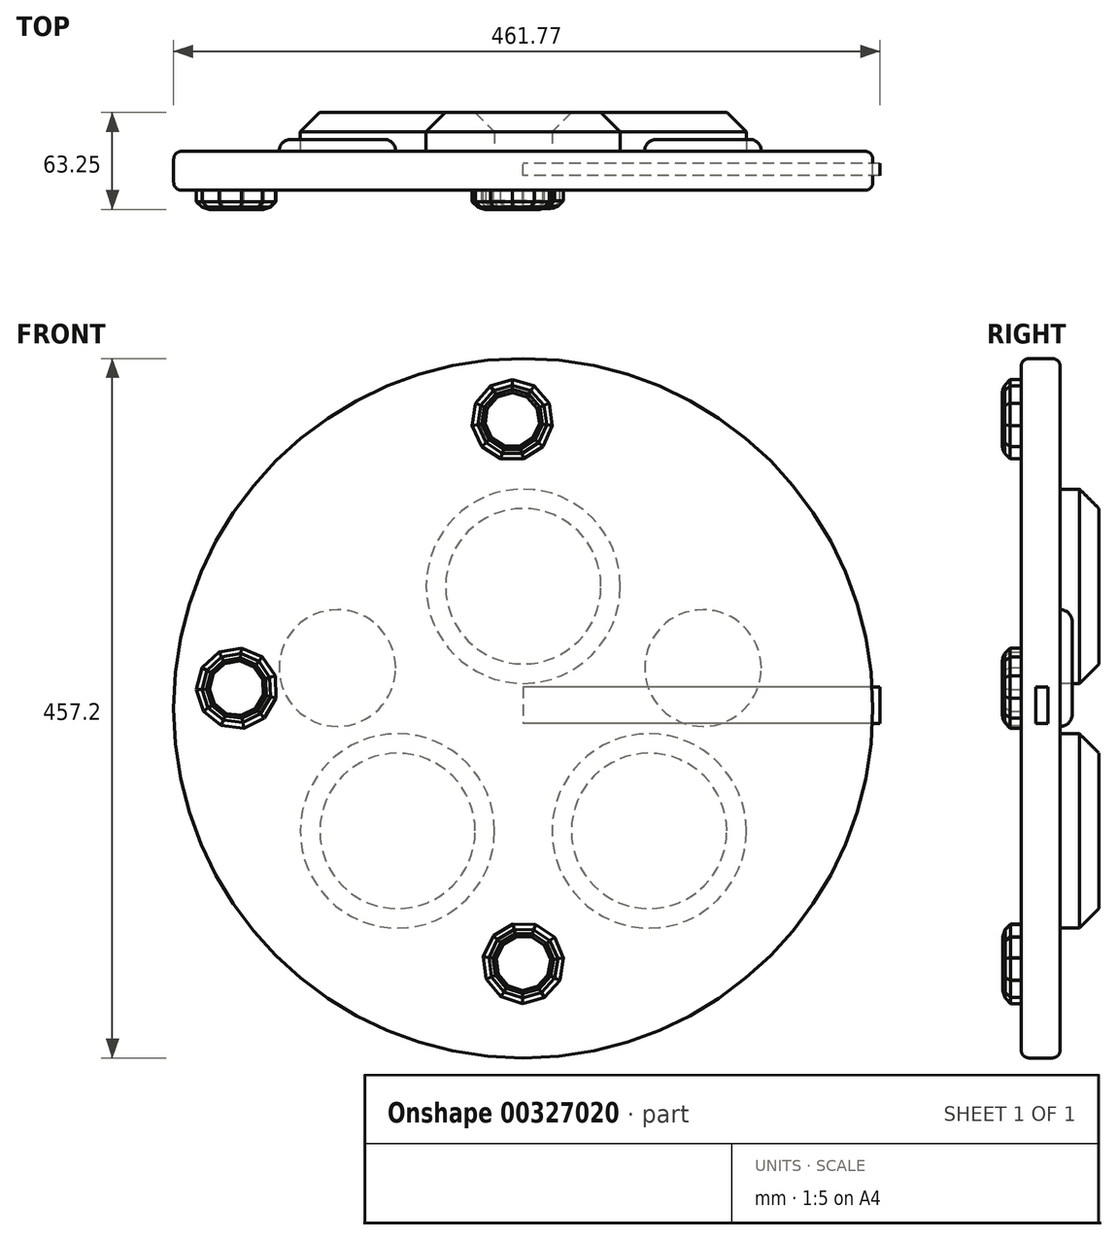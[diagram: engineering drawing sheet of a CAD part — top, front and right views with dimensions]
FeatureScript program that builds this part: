
annotation { "Feature Type Name" : "Feature", "Feature Type Description" : "" }
export const myFeature = defineFeature(function(context is Context, id is Id, definition is map)
    precondition{}
    {
        {
            var Q0;
            Q0=qCreatedBy(makeId("Front.planeOp"),FACE);
            var sketch = newSketch(context, id + "F0", { "sketchPlane" : qUnion([Q0])});
            skCircle(sketch, "E0", {"center": v(0, 0) * mm, "radius": 228.6 * mm});
            skSolve(sketch);
        }
        {
            var Q0;
            Q0 = qSketchRegion(id + "F0", true);
            extrude(context, id + "F1", {"entities" : qUnion([Q0]), "depth" : 25.4 * mm});
        }
        {
            var Q0;
            Q0=makeQuery(id+"F1.opExtrude","CAP_EDGE",EDGE,{"disambiguationData":[OSD([sQuery(id+"F0.wireOp",EDGE,"E0")])],"isStart":true});
            var Q1;
            Q1=makeQuery(id+"F1.opExtrude","CAP_EDGE",EDGE,{"disambiguationData":[OSD([sQuery(id+"F0.wireOp",EDGE,"E0")])],"isStart":false});
            fillet(context, id + "F2", {"entities" : qUnion([Q0, Q1]), "radius" : 5.08 * mm, "tangentPropagation" : true, "allowEdgeOverflow" : false});
        }
        {
            var Q0;
            Q0=makeQuery(id+"F1.opExtrude","CAP_FACE",FACE,{"disambiguationData":[OSD([sQuery(id+"F0.wireOp",EDGE,"E0")])],"isStart":true});
            var sketch = newSketch(context, id + "F3", { "sketchPlane" : qUnion([Q0])});
            skCircle(sketch, "E1", {"center": v(82.24, -80.23) * mm, "radius": 63.5 * mm});
            skCircle(sketch, "E2", {"center": v(-82.3, -80.23) * mm, "radius": 63.5 * mm});
            skCircle(sketch, "E3", {"center": v(0, 79.72) * mm, "radius": 63.5 * mm});
            skSolve(sketch);
        }
        {
            var Q0;
            Q0 = qSketchRegion(id + "F3", true);
            extrude(context, id + "F4", {"entities" : qUnion([Q0]), "depth" : 25.4 * mm});
        }
        {
            var Q0;
            Q0=qCreatedBy(makeId("Right.planeOp"),FACE);
            var sketch = newSketch(context, id + "F5", { "sketchPlane" : qUnion([Q0])});
            skLineSegment(sketch, "E4", {"start": v(-7.92, 13.98) * mm, "end": v(-7.92, -10.03) * mm});
            skLineSegment(sketch, "E5", {"start": v(-7.92, -10.03) * mm, "end": v(-15.92, -10.03) * mm});
            skLineSegment(sketch, "E6", {"start": v(-15.92, -10.03) * mm, "end": v(-15.92, 13.98) * mm});
            skLineSegment(sketch, "E7", {"start": v(-15.92, 13.98) * mm, "end": v(-7.92, 13.98) * mm});
            skSolve(sketch);
        }
        {
            var Q0;
            Q0 = qSketchRegion(id + "F5", true);
            extrude(context, id + "F6", {"entities" : qUnion([Q0]), "depth" : 233.17 * mm});
        }
        {
            var Q0;
            Q0=makeQuery(id+"F1.opExtrude","CAP_FACE",FACE,{"disambiguationData":[OSD([sQuery(id+"F0.wireOp",EDGE,"E0")])],"isStart":true});
            var sketch = newSketch(context, id + "F7", { "sketchPlane" : qUnion([Q0])});
            skCircle(sketch, "E8", {"center": v(121.52, 26.24) * mm, "radius": 38.1 * mm});
            skCircle(sketch, "E9", {"center": v(-117.51, 26.24) * mm, "radius": 38.1 * mm});
            skSolve(sketch);
        }
        {
            var Q0;
            Q0 = qSketchRegion(id + "F7", true);
            extrude(context, id + "F8", {"entities" : qUnion([Q0]), "depth" : 7.87 * mm});
        }
        {
            var Q0;
            Q0=makeQuery(id+"F4.opExtrude","CAP_EDGE",EDGE,{"disambiguationData":[OSD([sQuery(id+"F3.wireOp",EDGE,"E3")])],"isStart":false});
            var Q1;
            Q1=makeQuery(id+"F4.opExtrude","CAP_EDGE",EDGE,{"disambiguationData":[OSD([sQuery(id+"F3.wireOp",EDGE,"E2")])],"isStart":false});
            var Q2;
            Q2=makeQuery(id+"F4.opExtrude","CAP_EDGE",EDGE,{"disambiguationData":[OSD([sQuery(id+"F3.wireOp",EDGE,"E1")])],"isStart":false});
            chamfer(context, id + "F9", {"entities" : qUnion([Q0, Q1, Q2]), "width" : 12.7 * mm, "tangentPropagation" : true});
        }
        {
            var Q0;
            Q0=makeQuery(id+"F1.opExtrude","CAP_FACE",FACE,{"disambiguationData":[OSD([sQuery(id+"F0.wireOp",EDGE,"E0")])],"isStart":false});
            var sketch = newSketch(context, id + "F10", { "sketchPlane" : qUnion([Q0])});
            skCircle(sketch, "E10.cCircle", {"center": v(-187.32, 13.07) * mm, "radius": 25.4 * mm, "construction": true});
            skLineSegment(sketch, "E10.0", {"start": v(-161.7, 6.4) * mm, "end": v(-169.38, -6.4) * mm});
            skLineSegment(sketch, "E10.1", {"start": v(-169.38, -6.4) * mm, "end": v(-182.75, -13) * mm});
            skLineSegment(sketch, "E10.2", {"start": v(-182.75, -13) * mm, "end": v(-197.57, -11.33) * mm});
            skLineSegment(sketch, "E10.3", {"start": v(-197.57, -11.33) * mm, "end": v(-209.14, -1.91) * mm});
            skLineSegment(sketch, "E10.4", {"start": v(-209.14, -1.91) * mm, "end": v(-213.78, 12.27) * mm});
            skLineSegment(sketch, "E10.5", {"start": v(-213.78, 12.27) * mm, "end": v(-210.01, 26.7) * mm});
            skLineSegment(sketch, "E10.6", {"start": v(-210.01, 26.7) * mm, "end": v(-199.04, 36.8) * mm});
            skLineSegment(sketch, "E10.7", {"start": v(-199.04, 36.8) * mm, "end": v(-184.35, 39.38) * mm});
            skLineSegment(sketch, "E10.8", {"start": v(-184.35, 39.38) * mm, "end": v(-170.6, 33.6) * mm});
            skLineSegment(sketch, "E10.9", {"start": v(-170.6, 33.6) * mm, "end": v(-162.15, 21.3) * mm});
            skLineSegment(sketch, "E10.10", {"start": v(-162.15, 21.3) * mm, "end": v(-161.7, 6.4) * mm});
            skPoint(sketch, "E10.0.midPoint", {"position": v(-165.54, 0) * mm});
            skSolve(sketch);
        }
        {
            var Q0;
            Q0=makeQuery(id+"F10.imprint","IMPRINT",FACE,{"disambiguationData":[TD([[makeQuery(id+"F10.imprint","IMPRINT",EDGE,{"derivedFrom":sQuery(id+"F10.wireOp",EDGE,"E10.0")}),-1.0]])]});
            extrude(context, id + "F11", {"entities" : qUnion([Q0]), "depth" : 12.45 * mm});
        }
        {
            var Q0;
            Q0=makeQuery(id+"F11.opExtrude","CAP_FACE",FACE,{"disambiguationData":[OSD([sQuery(id+"F10.wireOp",EDGE,"E10.0"),sQuery(id+"F10.wireOp",EDGE,"E10.1"),sQuery(id+"F10.wireOp",EDGE,"E10.2"),sQuery(id+"F10.wireOp",EDGE,"E10.3"),sQuery(id+"F10.wireOp",EDGE,"E10.4"),sQuery(id+"F10.wireOp",EDGE,"E10.5"),sQuery(id+"F10.wireOp",EDGE,"E10.6"),sQuery(id+"F10.wireOp",EDGE,"E10.7"),sQuery(id+"F10.wireOp",EDGE,"E10.8"),sQuery(id+"F10.wireOp",EDGE,"E10.9"),sQuery(id+"F10.wireOp",EDGE,"E10.10")])],"isStart":false});
            chamfer(context, id + "F12", {"entities" : qUnion([Q0]), "width" : 5.08 * mm, "tangentPropagation" : true});
        }
        {
            var Q0;
            Q0=makeQuery(id+"F11.opExtrude","CAP_FACE",FACE,{"disambiguationData":[OSD([sQuery(id+"F10.wireOp",EDGE,"E10.0"),sQuery(id+"F10.wireOp",EDGE,"E10.1"),sQuery(id+"F10.wireOp",EDGE,"E10.2"),sQuery(id+"F10.wireOp",EDGE,"E10.3"),sQuery(id+"F10.wireOp",EDGE,"E10.4"),sQuery(id+"F10.wireOp",EDGE,"E10.5"),sQuery(id+"F10.wireOp",EDGE,"E10.6"),sQuery(id+"F10.wireOp",EDGE,"E10.7"),sQuery(id+"F10.wireOp",EDGE,"E10.8"),sQuery(id+"F10.wireOp",EDGE,"E10.9"),sQuery(id+"F10.wireOp",EDGE,"E10.10")])],"isStart":false});
            chamfer(context, id + "F13", {"entities" : qUnion([Q0]), "width" : 5.08 * mm, "tangentPropagation" : true});
        }
        {
            var Q0;
            Q0=makeQuery(id+"F11.opExtrude","CAP_FACE",FACE,{"disambiguationData":[OSD([sQuery(id+"F10.wireOp",EDGE,"E10.0"),sQuery(id+"F10.wireOp",EDGE,"E10.1"),sQuery(id+"F10.wireOp",EDGE,"E10.2"),sQuery(id+"F10.wireOp",EDGE,"E10.3"),sQuery(id+"F10.wireOp",EDGE,"E10.4"),sQuery(id+"F10.wireOp",EDGE,"E10.5"),sQuery(id+"F10.wireOp",EDGE,"E10.6"),sQuery(id+"F10.wireOp",EDGE,"E10.7"),sQuery(id+"F10.wireOp",EDGE,"E10.8"),sQuery(id+"F10.wireOp",EDGE,"E10.9"),sQuery(id+"F10.wireOp",EDGE,"E10.10")])],"isStart":false});
            chamfer(context, id + "F14", {"entities" : qUnion([Q0]), "width" : 5.08 * mm, "tangentPropagation" : true});
        }
        {
            var Q0;
            Q0=makeQuery(id+"F1.opExtrude","CAP_FACE",FACE,{"disambiguationData":[OSD([sQuery(id+"F0.wireOp",EDGE,"E0")])],"isStart":false});
            var sketch = newSketch(context, id + "F15", { "sketchPlane" : qUnion([Q0])});
            skCircle(sketch, "E11.cCircle", {"center": v(-7.24, 188.4) * mm, "radius": 25.4 * mm, "construction": true});
            skLineSegment(sketch, "E11.0", {"start": v(0.22, 163) * mm, "end": v(-14.7, 163) * mm});
            skLineSegment(sketch, "E11.1", {"start": v(-14.7, 163) * mm, "end": v(-27.24, 171.07) * mm});
            skLineSegment(sketch, "E11.2", {"start": v(-27.24, 171.07) * mm, "end": v(-33.44, 184.64) * mm});
            skLineSegment(sketch, "E11.3", {"start": v(-33.44, 184.64) * mm, "end": v(-31.32, 199.4) * mm});
            skLineSegment(sketch, "E11.4", {"start": v(-31.32, 199.4) * mm, "end": v(-21.55, 210.68) * mm});
            skLineSegment(sketch, "E11.5", {"start": v(-21.55, 210.68) * mm, "end": v(-7.24, 214.88) * mm});
            skLineSegment(sketch, "E11.6", {"start": v(-7.24, 214.88) * mm, "end": v(7.07, 210.68) * mm});
            skLineSegment(sketch, "E11.7", {"start": v(7.07, 210.68) * mm, "end": v(16.84, 199.4) * mm});
            skLineSegment(sketch, "E11.8", {"start": v(16.84, 199.4) * mm, "end": v(18.96, 184.64) * mm});
            skLineSegment(sketch, "E11.9", {"start": v(18.96, 184.64) * mm, "end": v(12.77, 171.07) * mm});
            skLineSegment(sketch, "E11.10", {"start": v(12.77, 171.07) * mm, "end": v(0.22, 163) * mm});
            skPoint(sketch, "E11.0.midPoint", {"position": v(-7.24, 163) * mm});
            skSolve(sketch);
        }
        {
            var Q0;
            Q0=makeQuery(id+"F15.imprint","IMPRINT",FACE,{"disambiguationData":[TD([[makeQuery(id+"F15.imprint","IMPRINT",EDGE,{"derivedFrom":sQuery(id+"F15.wireOp",EDGE,"E11.0")}),-1.0]])]});
            extrude(context, id + "F16", {"entities" : qUnion([Q0]), "depth" : 12.45 * mm});
        }
        {
            var Q0;
            Q0=makeQuery(id+"F16.opExtrude","CAP_FACE",FACE,{"disambiguationData":[OSD([sQuery(id+"F15.wireOp",EDGE,"E11.0"),sQuery(id+"F15.wireOp",EDGE,"E11.1"),sQuery(id+"F15.wireOp",EDGE,"E11.2"),sQuery(id+"F15.wireOp",EDGE,"E11.3"),sQuery(id+"F15.wireOp",EDGE,"E11.4"),sQuery(id+"F15.wireOp",EDGE,"E11.5"),sQuery(id+"F15.wireOp",EDGE,"E11.6"),sQuery(id+"F15.wireOp",EDGE,"E11.7"),sQuery(id+"F15.wireOp",EDGE,"E11.8"),sQuery(id+"F15.wireOp",EDGE,"E11.9"),sQuery(id+"F15.wireOp",EDGE,"E11.10")])],"isStart":false});
            chamfer(context, id + "F17", {"entities" : qUnion([Q0]), "width" : 5.08 * mm, "tangentPropagation" : true});
        }
        {
            var Q0;
            Q0=makeQuery(id+"F16.opExtrude","CAP_FACE",FACE,{"disambiguationData":[OSD([sQuery(id+"F15.wireOp",EDGE,"E11.0"),sQuery(id+"F15.wireOp",EDGE,"E11.1"),sQuery(id+"F15.wireOp",EDGE,"E11.2"),sQuery(id+"F15.wireOp",EDGE,"E11.3"),sQuery(id+"F15.wireOp",EDGE,"E11.4"),sQuery(id+"F15.wireOp",EDGE,"E11.5"),sQuery(id+"F15.wireOp",EDGE,"E11.6"),sQuery(id+"F15.wireOp",EDGE,"E11.7"),sQuery(id+"F15.wireOp",EDGE,"E11.8"),sQuery(id+"F15.wireOp",EDGE,"E11.9"),sQuery(id+"F15.wireOp",EDGE,"E11.10")])],"isStart":false});
            chamfer(context, id + "F18", {"entities" : qUnion([Q0]), "width" : 5.08 * mm, "tangentPropagation" : true});
        }
        {
            var Q0;
            Q0=makeQuery(id+"F16.opExtrude","CAP_FACE",FACE,{"disambiguationData":[OSD([sQuery(id+"F15.wireOp",EDGE,"E11.0"),sQuery(id+"F15.wireOp",EDGE,"E11.1"),sQuery(id+"F15.wireOp",EDGE,"E11.2"),sQuery(id+"F15.wireOp",EDGE,"E11.3"),sQuery(id+"F15.wireOp",EDGE,"E11.4"),sQuery(id+"F15.wireOp",EDGE,"E11.5"),sQuery(id+"F15.wireOp",EDGE,"E11.6"),sQuery(id+"F15.wireOp",EDGE,"E11.7"),sQuery(id+"F15.wireOp",EDGE,"E11.8"),sQuery(id+"F15.wireOp",EDGE,"E11.9"),sQuery(id+"F15.wireOp",EDGE,"E11.10")])],"isStart":false});
            chamfer(context, id + "F19", {"entities" : qUnion([Q0]), "width" : 5.08 * mm, "tangentPropagation" : true});
        }
        {
            var Q0;
            Q0=makeQuery(id+"F8.opExtrude","CAP_EDGE",EDGE,{"disambiguationData":[OSD([sQuery(id+"F7.wireOp",EDGE,"E8")])],"isStart":false});
            var Q1;
            Q1=makeQuery(id+"F8.opExtrude","CAP_EDGE",EDGE,{"disambiguationData":[OSD([sQuery(id+"F7.wireOp",EDGE,"E9")])],"isStart":false});
            fillet(context, id + "F20", {"entities" : qUnion([Q0, Q1]), "radius" : 7.62 * mm, "tangentPropagation" : true, "allowEdgeOverflow" : false});
        }
        {
            var Q0;
            Q0=makeQuery(id+"F1.opExtrude","CAP_FACE",FACE,{"disambiguationData":[OSD([sQuery(id+"F0.wireOp",EDGE,"E0")])],"isStart":false});
            var sketch = newSketch(context, id + "F21", { "sketchPlane" : qUnion([Q0])});
            skCircle(sketch, "E12.cCircle", {"center": v(0, -166.57) * mm, "radius": 25.4 * mm, "construction": true});
            skLineSegment(sketch, "E12.0", {"start": v(20.35, -149.63) * mm, "end": v(26.27, -163.32) * mm});
            skLineSegment(sketch, "E12.1", {"start": v(26.27, -163.32) * mm, "end": v(23.86, -178.04) * mm});
            skLineSegment(sketch, "E12.2", {"start": v(23.86, -178.04) * mm, "end": v(13.87, -189.12) * mm});
            skLineSegment(sketch, "E12.3", {"start": v(13.87, -189.12) * mm, "end": v(-0.52, -193.04) * mm});
            skLineSegment(sketch, "E12.4", {"start": v(-0.52, -193.04) * mm, "end": v(-14.75, -188.55) * mm});
            skLineSegment(sketch, "E12.5", {"start": v(-14.75, -188.55) * mm, "end": v(-24.3, -177.09) * mm});
            skLineSegment(sketch, "E12.6", {"start": v(-24.3, -177.09) * mm, "end": v(-26.12, -162.28) * mm});
            skLineSegment(sketch, "E12.7", {"start": v(-26.12, -162.28) * mm, "end": v(-19.66, -148.84) * mm});
            skLineSegment(sketch, "E12.8", {"start": v(-19.66, -148.84) * mm, "end": v(-6.95, -141.03) * mm});
            skLineSegment(sketch, "E12.9", {"start": v(-6.95, -141.03) * mm, "end": v(7.96, -141.32) * mm});
            skLineSegment(sketch, "E12.10", {"start": v(7.96, -141.32) * mm, "end": v(20.35, -149.63) * mm});
            skPoint(sketch, "E12.0.midPoint", {"position": v(23.3, -156.48) * mm});
            skSolve(sketch);
        }
        {
            var Q0;
            Q0=makeQuery(id+"F21.imprint","IMPRINT",FACE,{"disambiguationData":[TD([[makeQuery(id+"F21.imprint","IMPRINT",EDGE,{"derivedFrom":sQuery(id+"F21.wireOp",EDGE,"E12.0")}),-1.0]])]});
            extrude(context, id + "F22", {"entities" : qUnion([Q0]), "depth" : 11.94 * mm});
        }
        {
            var Q0;
            Q0=makeQuery(id+"F22.opExtrude","CAP_FACE",FACE,{"disambiguationData":[OSD([sQuery(id+"F21.wireOp",EDGE,"E12.0"),sQuery(id+"F21.wireOp",EDGE,"E12.1"),sQuery(id+"F21.wireOp",EDGE,"E12.2"),sQuery(id+"F21.wireOp",EDGE,"E12.3"),sQuery(id+"F21.wireOp",EDGE,"E12.4"),sQuery(id+"F21.wireOp",EDGE,"E12.5"),sQuery(id+"F21.wireOp",EDGE,"E12.6"),sQuery(id+"F21.wireOp",EDGE,"E12.7"),sQuery(id+"F21.wireOp",EDGE,"E12.8"),sQuery(id+"F21.wireOp",EDGE,"E12.9"),sQuery(id+"F21.wireOp",EDGE,"E12.10")])],"isStart":false});
            chamfer(context, id + "F23", {"entities" : qUnion([Q0]), "width" : 5.08 * mm, "tangentPropagation" : true});
        }
        {
            var Q0;
            Q0=makeQuery(id+"F22.opExtrude","CAP_FACE",FACE,{"disambiguationData":[OSD([sQuery(id+"F21.wireOp",EDGE,"E12.0"),sQuery(id+"F21.wireOp",EDGE,"E12.1"),sQuery(id+"F21.wireOp",EDGE,"E12.2"),sQuery(id+"F21.wireOp",EDGE,"E12.3"),sQuery(id+"F21.wireOp",EDGE,"E12.4"),sQuery(id+"F21.wireOp",EDGE,"E12.5"),sQuery(id+"F21.wireOp",EDGE,"E12.6"),sQuery(id+"F21.wireOp",EDGE,"E12.7"),sQuery(id+"F21.wireOp",EDGE,"E12.8"),sQuery(id+"F21.wireOp",EDGE,"E12.9"),sQuery(id+"F21.wireOp",EDGE,"E12.10")])],"isStart":false});
            chamfer(context, id + "F24", {"entities" : qUnion([Q0]), "width" : 5.08 * mm, "tangentPropagation" : true});
        }
        {
            var Q0;
            Q0=makeQuery(id+"F22.opExtrude","CAP_FACE",FACE,{"disambiguationData":[OSD([sQuery(id+"F21.wireOp",EDGE,"E12.0"),sQuery(id+"F21.wireOp",EDGE,"E12.1"),sQuery(id+"F21.wireOp",EDGE,"E12.2"),sQuery(id+"F21.wireOp",EDGE,"E12.3"),sQuery(id+"F21.wireOp",EDGE,"E12.4"),sQuery(id+"F21.wireOp",EDGE,"E12.5"),sQuery(id+"F21.wireOp",EDGE,"E12.6"),sQuery(id+"F21.wireOp",EDGE,"E12.7"),sQuery(id+"F21.wireOp",EDGE,"E12.8"),sQuery(id+"F21.wireOp",EDGE,"E12.9"),sQuery(id+"F21.wireOp",EDGE,"E12.10")])],"isStart":false});
            chamfer(context, id + "F25", {"entities" : qUnion([Q0]), "width" : 5.08 * mm, "tangentPropagation" : true});
        }
    });
